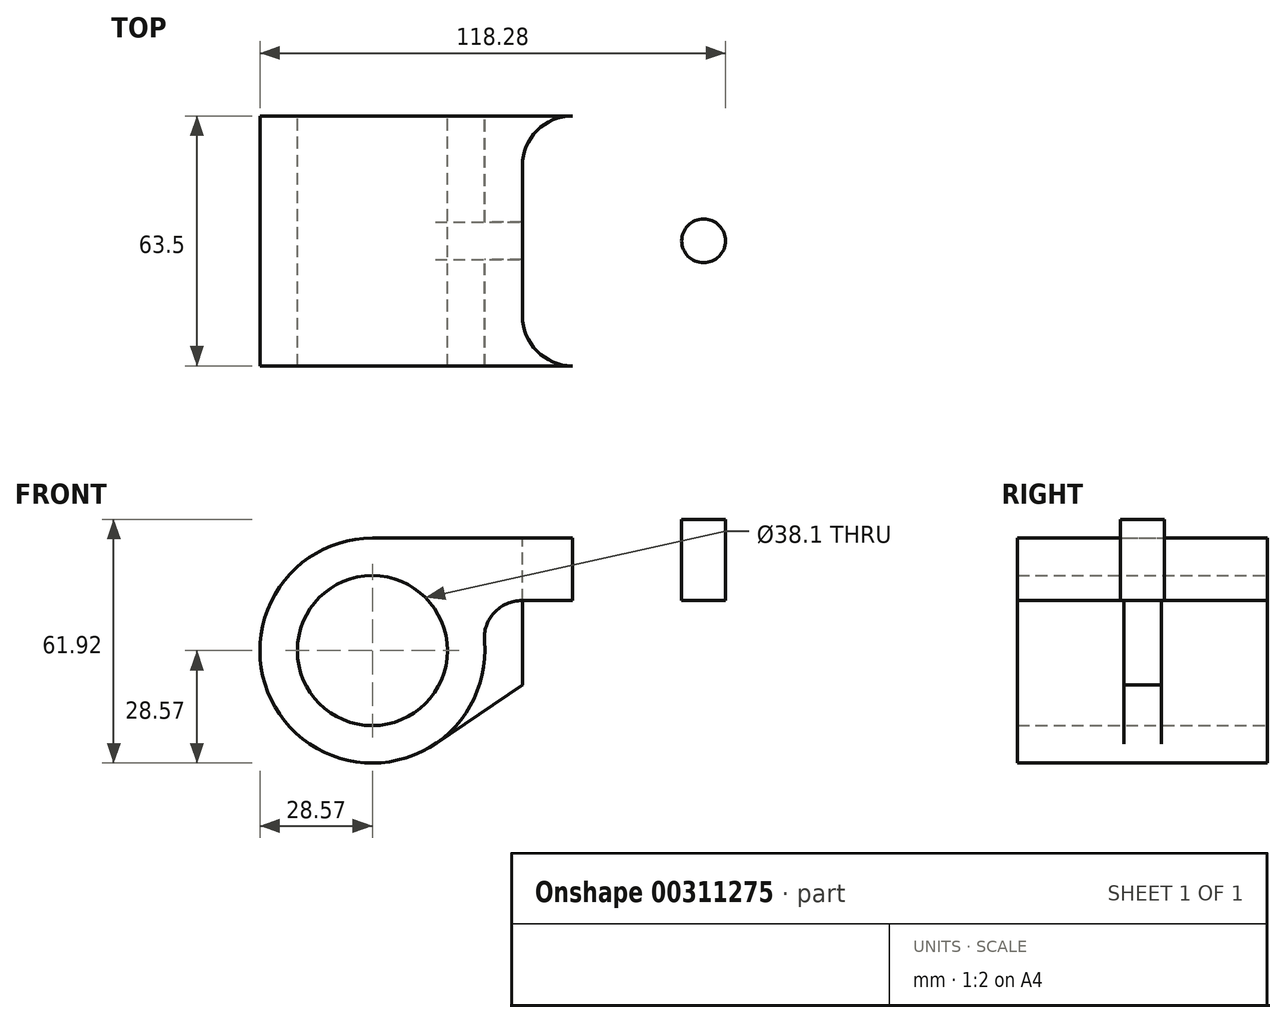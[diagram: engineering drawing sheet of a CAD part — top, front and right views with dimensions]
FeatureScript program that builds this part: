
annotation { "Feature Type Name" : "Feature", "Feature Type Description" : "" }
export const myFeature = defineFeature(function(context is Context, id is Id, definition is map)
    precondition{}
    {
        {
            var Q0;
            Q0=qCreatedBy(makeId("Front.planeOp"),FACE);
            var sketch = newSketch(context, id + "F0", { "sketchPlane" : qUnion([Q0])});
            skCircle(sketch, "E0", {"center": v(0, 0) * mm, "radius": 19.05 * mm});
            skLineSegment(sketch, "E1", {"start": v(0, 28.58) * mm, "end": v(50.8, 28.58) * mm});
            skLineSegment(sketch, "E2", {"start": v(96.85, 33.35) * mm, "end": v(96.85, 12.7) * mm});
            skLineSegment(sketch, "E3", {"start": v(96.85, 12.7) * mm, "end": v(37.97, 12.7) * mm});
            skArc(sketch, "E4", {"start": v(0, 28.58) * mm, "mid": v(-19.35, -21.03) * mm, "end": v(28.48, 2.38) * mm});
            skArc(sketch, "E5", {"start": v(37.97, 12.7) * mm, "mid": v(30.96, 9.62) * mm, "end": v(28.48, 2.38) * mm});
            skLineSegment(sketch, "E6", {"start": v(96.85, 33.35) * mm, "end": v(38.1, 33.35) * mm});
            skLineSegment(sketch, "E7", {"start": v(38.1, 33.35) * mm, "end": v(38.1, 28.58) * mm});
            skLineSegment(sketch, "E8", {"start": v(16, -23.68) * mm, "end": v(69.85, 12.7) * mm});
            skSolve(sketch);
        }
        {
            var Q0;
            {var subQ0=sQuery(id+"F0.wireOp",EDGE,"E5");Q0=makeQuery(id+"F0.imprint","IMPRINT",FACE,{"disambiguationData":[TD([[makeQuery(id+"F0.imprint","IMPRINT",EDGE,{"derivedFrom":subQ0}),1.0]])]});}
            extrude(context, id + "F1", {"entities" : qUnion([Q0]), "depth" : 9.52 * mm, "symmetric" : true});
        }
        {
            var Q0;
            Q0=makeQuery(id+"F0.imprint","IMPRINT",FACE,{"disambiguationData":[TD([[makeQuery(id+"F0.imprint","IMPRINT",EDGE,{"derivedFrom":sQuery(id+"F0.wireOp",EDGE,"E0")}),-1.0]])]});
            extrude(context, id + "F2", {"entities" : qUnion([Q0]), "operationType" : NewBodyOperationType.ADD, "depth" : 63.5 * mm, "symmetric" : true});
        }
        {
            var Q0;
            Q0=makeQuery(id+"F2.opExtrude","SWEPT_FACE",FACE,{"disambiguationData":[OSD([sQuery(id+"F0.wireOp",EDGE,"E6")])]});
            var sketch = newSketch(context, id + "F3", { "sketchPlane" : qUnion([Q0])});
            skPoint(sketch, "E9.0", {"position": v(50.8, 0) * mm});
            skLineSegment(sketch, "E10.0", {"start": v(38.1, -31.75) * mm, "end": v(38.1, 31.75) * mm});
            skLineSegment(sketch, "E11.0", {"start": v(96.85, 0) * mm, "end": v(38.1, 0) * mm});
            skLineSegment(sketch, "E12", {"start": v(50.8, 19.05) * mm, "end": v(50.8, -19.05) * mm, "construction": true});
            skCircle(sketch, "E13", {"center": v(50.8, -19.05) * mm, "radius": 5.56 * mm});
            skCircle(sketch, "E14", {"center": v(50.8, 19.05) * mm, "radius": 5.56 * mm});
            skCircle(sketch, "E15", {"center": v(84.15, 0) * mm, "radius": 5.56 * mm});
            skArc(sketch, "E16", {"start": v(38.1, 19.05) * mm, "mid": v(44.42, 30.03) * mm, "end": v(57.1, 30.08) * mm});
            skArc(sketch, "E17", {"start": v(38.1, -19.05) * mm, "mid": v(44.42, -30.03) * mm, "end": v(57.1, -30.08) * mm});
            skArc(sketch, "E18", {"start": v(90.45, 11.03) * mm, "mid": v(96.85, 0) * mm, "end": v(90.45, -11.03) * mm});
            skLineSegment(sketch, "E19", {"start": v(90.45, 11.03) * mm, "end": v(57.1, 30.08) * mm});
            skLineSegment(sketch, "E20", {"start": v(90.45, -11.03) * mm, "end": v(57.1, -30.08) * mm});
            skLineSegment(sketch, "E21", {"start": v(38.1, 19.05) * mm, "end": v(38.1, -19.05) * mm});
            skSolve(sketch);
        }
        {
            var Q0;
            {var subQ0=sQuery(id+"F3.wireOp",EDGE,"E19");Q0=makeQuery(id+"F3.imprint","IMPRINT",FACE,{"disambiguationData":[TD([[makeQuery(id+"F3.imprint","IMPRINT",EDGE,{"derivedFrom":subQ0}),-1.0]])]});}
            var Q1;
            {var subQ0=sQuery(id+"F3.wireOp",EDGE,"E20");Q1=makeQuery(id+"F3.imprint","IMPRINT",FACE,{"disambiguationData":[TD([[makeQuery(id+"F3.imprint","IMPRINT",EDGE,{"derivedFrom":subQ0}),1.0]])]});}
            extrude(context, id + "F4", {"entities" : qUnion([Q0, Q1]), "operationType" : NewBodyOperationType.REMOVE, "endBound" : BoundingType.THROUGH_ALL, "oppositeDirection" : true, "depth" : 25.4 * mm});
        }
        {
            var Q0;
            {var subQ0=sQuery(id+"F3.wireOp",EDGE,"E10.0");var subQ1=makeQuery(id+"F2.opExtrude","CAP_EDGE",EDGE,{"disambiguationData":[OSD([sQuery(id+"F0.wireOp",EDGE,"E6")])],"isStart":false});var subQ2=makeQuery(id+"F3.imprint","INTERSECT",VERTEX,{"derivedFrom":[subQ1,subQ0]});Q0=makeQuery(id+"F3.imprint","IMPRINT",FACE,{"disambiguationData":[TD([[makeQuery(id+"F3.imprint","IMPRINT",EDGE,{"disambiguationData":[TD([[subQ2,1.0]])],"derivedFrom":subQ1}),-1.0]])]});}
            var Q1;
            {var subQ0=sQuery(id+"F3.wireOp",EDGE,"E10.0");var subQ1=makeQuery(id+"F2.opExtrude","CAP_EDGE",EDGE,{"disambiguationData":[OSD([sQuery(id+"F0.wireOp",EDGE,"E6")])],"isStart":true});var subQ2=makeQuery(id+"F3.imprint","INTERSECT",VERTEX,{"derivedFrom":[subQ1,subQ0]});Q1=makeQuery(id+"F3.imprint","IMPRINT",FACE,{"disambiguationData":[TD([[makeQuery(id+"F3.imprint","IMPRINT",EDGE,{"disambiguationData":[TD([[subQ2,1.0]])],"derivedFrom":subQ1}),1.0]])]});}
            extrude(context, id + "F5", {"entities" : qUnion([Q0, Q1]), "operationType" : NewBodyOperationType.REMOVE, "oppositeDirection" : true, "depth" : 4.78 * mm});
        }
        {
            var Q0;
            Q0=makeQuery(id+"F3.imprint","IMPRINT",FACE,{"disambiguationData":[TD([[makeQuery(id+"F3.imprint","IMPRINT",EDGE,{"derivedFrom":sQuery(id+"F3.wireOp",EDGE,"E14")}),1.0]])]});
            var Q1;
            Q1=makeQuery(id+"F3.imprint","IMPRINT",FACE,{"disambiguationData":[TD([[makeQuery(id+"F3.imprint","IMPRINT",EDGE,{"derivedFrom":sQuery(id+"F3.wireOp",EDGE,"E13")}),1.0]])]});
            var Q2;
            {var subQ0=sQuery(id+"F3.wireOp",EDGE,"E15");var subQ1=sQuery(id+"F3.wireOp",EDGE,"E11.0");var subQ2=makeQuery(id+"F3.imprint","INTERSECT",VERTEX,{"disambiguationData":[OD(0.0)],"derivedFrom":[subQ1,subQ0]});Q2=makeQuery(id+"F3.imprint","IMPRINT",FACE,{"disambiguationData":[TD([[makeQuery(id+"F3.imprint","IMPRINT",EDGE,{"disambiguationData":[TD([[subQ2,-1.0]])],"derivedFrom":subQ1}),1.0]])]});}
            var Q3;
            {var subQ0=sQuery(id+"F3.wireOp",EDGE,"E15");var subQ1=sQuery(id+"F3.wireOp",EDGE,"E11.0");var subQ2=makeQuery(id+"F3.imprint","INTERSECT",VERTEX,{"disambiguationData":[OD(0.0)],"derivedFrom":[subQ1,subQ0]});Q3=makeQuery(id+"F3.imprint","IMPRINT",FACE,{"disambiguationData":[TD([[makeQuery(id+"F3.imprint","IMPRINT",EDGE,{"disambiguationData":[TD([[subQ2,-1.0]])],"derivedFrom":subQ1}),-1.0]])]});}
            extrude(context, id + "F6", {"entities" : qUnion([Q0, Q1, Q2, Q3]), "operationType" : NewBodyOperationType.REMOVE, "endBound" : BoundingType.THROUGH_ALL, "oppositeDirection" : true, "depth" : 25.4 * mm});
        }
    });
